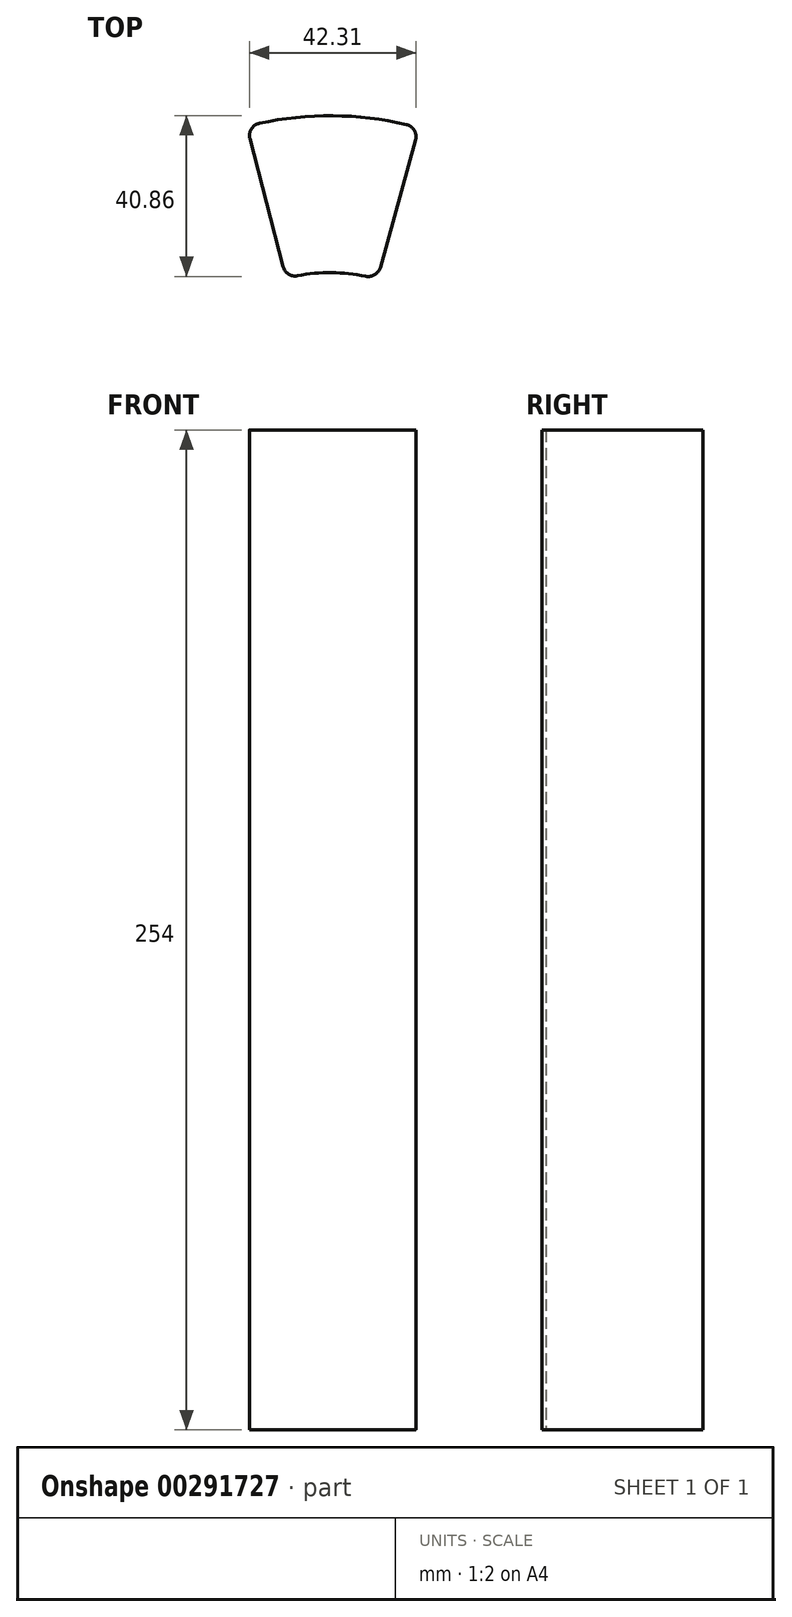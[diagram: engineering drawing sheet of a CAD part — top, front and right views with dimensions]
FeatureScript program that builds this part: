
annotation { "Feature Type Name" : "Feature", "Feature Type Description" : "" }
export const myFeature = defineFeature(function(context is Context, id is Id, definition is map)
    precondition{}
    {
        {
            var Q0;
            Q0=qCreatedBy(makeId("Top.planeOp"),FACE);
            var sketch = newSketch(context, id + "F0", { "sketchPlane" : qUnion([Q0])});
            skArc(sketch, "E0", {"start": v(19.37, 82.3) * mm, "mid": v(0.7, 84.55) * mm, "end": v(-18, 82.62) * mm});
            skArc(sketch, "E1", {"start": v(9.04, 43.75) * mm, "mid": v(0.37, 44.67) * mm, "end": v(-8.3, 43.9) * mm});
            skLineSegment(sketch, "E2", {"start": v(12.74, 46.01) * mm, "end": v(21.7, 78.37) * mm});
            skLineSegment(sketch, "E3", {"start": v(-11.97, 46.22) * mm, "end": v(-20.39, 78.72) * mm});
            skPoint(sketch, "E4.visualSharp", {"position": v(-21.2, 81.85) * mm});
            skArc(sketch, "E4.filletArc", {"start": v(-18, 82.62) * mm, "mid": v(-20.02, 81.18) * mm, "end": v(-20.39, 78.72) * mm});
            skPoint(sketch, "E5.visualSharp", {"position": v(22.56, 81.49) * mm});
            skArc(sketch, "E5.filletArc", {"start": v(21.7, 78.37) * mm, "mid": v(21.37, 80.83) * mm, "end": v(19.37, 82.3) * mm});
            skPoint(sketch, "E6.visualSharp", {"position": v(-11.2, 43.25) * mm});
            skArc(sketch, "E6.filletArc", {"start": v(-11.97, 46.22) * mm, "mid": v(-10.6, 44.33) * mm, "end": v(-8.3, 43.9) * mm});
            skPoint(sketch, "E7.visualSharp", {"position": v(11.92, 43.05) * mm});
            skArc(sketch, "E7.filletArc", {"start": v(9.04, 43.75) * mm, "mid": v(11.34, 44.15) * mm, "end": v(12.74, 46.01) * mm});
            skSolve(sketch);
        }
        {
            var Q0;
            Q0 = qSketchRegion(id + "F0", true);
            extrude(context, id + "F1", {"entities" : qUnion([Q0]), "depth" : 254 * mm});
        }
    });
